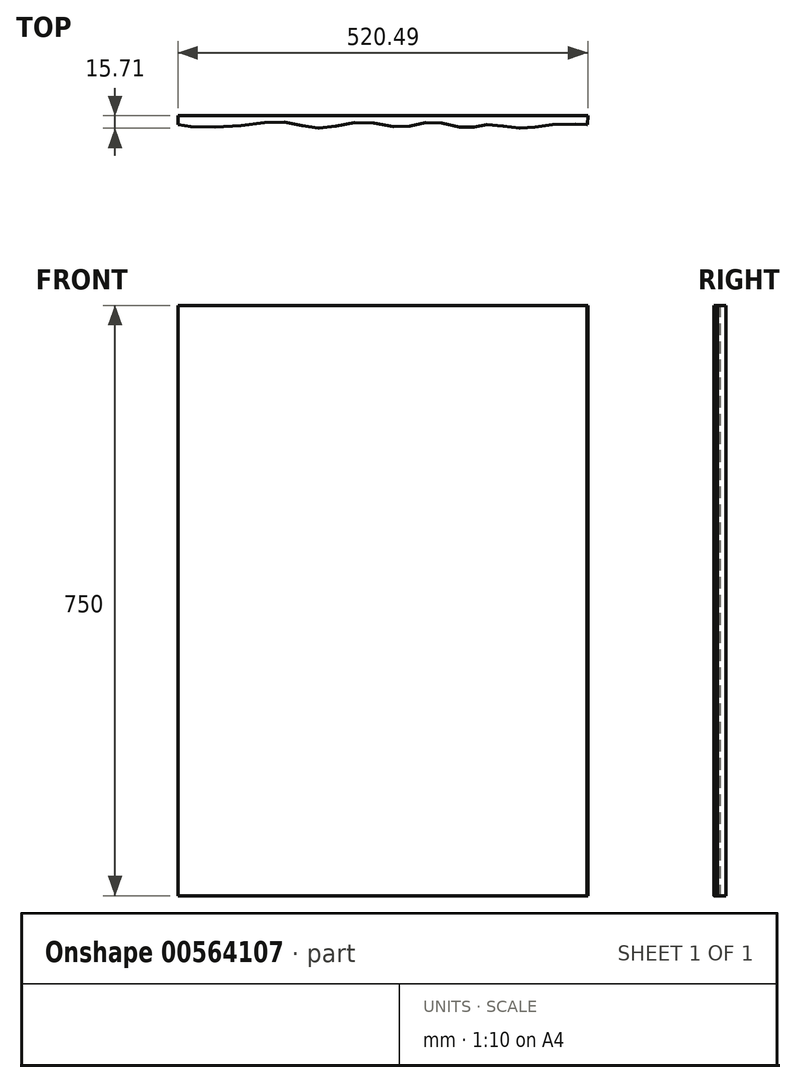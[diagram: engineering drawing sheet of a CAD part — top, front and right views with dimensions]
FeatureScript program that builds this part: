
annotation { "Feature Type Name" : "Feature", "Feature Type Description" : "" }
export const myFeature = defineFeature(function(context is Context, id is Id, definition is map)
    precondition{}
    {
        {
            var Q0;
            Q0=qCreatedBy(makeId("Top.planeOp"),FACE);
            var sketch = newSketch(context, id + "F0", { "sketchPlane" : qUnion([Q0])});
            skFitSpline(sketch, "E0", {"points": [v(-296.6, 0) * mm, v(-237.78, -3) * mm, v(-159.95, 3) * mm, v(-116.33, -4.5) * mm, v(-65.8, 3.21) * mm, v(-11.02, -3.01) * mm, v(25.79, 3.06) * mm, v(69.83, -3.94) * mm, v(96.9, 0) * mm, v(138, -4.45) * mm, v(178.32, 0) * mm, v(222.51, 0) * mm], "startDerivative": vector(103.8, -71.96) * mm, "endDerivative": vector(-29.84, -7.32) * mm});
            skLineSegment(sketch, "E1", {"start": v(-296.6, 0) * mm, "end": v(-296.6, 11.2) * mm});
            skLineSegment(sketch, "E2", {"start": v(-296.6, 11.2) * mm, "end": v(223.88, 11.2) * mm});
            skLineSegment(sketch, "E3", {"start": v(223.88, 11.2) * mm, "end": v(223.4, 0.22) * mm});
            skLineSegment(sketch, "E4", {"start": v(222.51, 0) * mm, "end": v(223.4, 0.22) * mm});
            skSolve(sketch);
        }
        {
            var Q0;
            Q0 = qSketchRegion(id + "F0", true);
            extrude(context, id + "F1", {"entities" : qUnion([Q0]), "depth" : 750 * mm, "offsetDistance" : 25 * mm});
        }
    });
